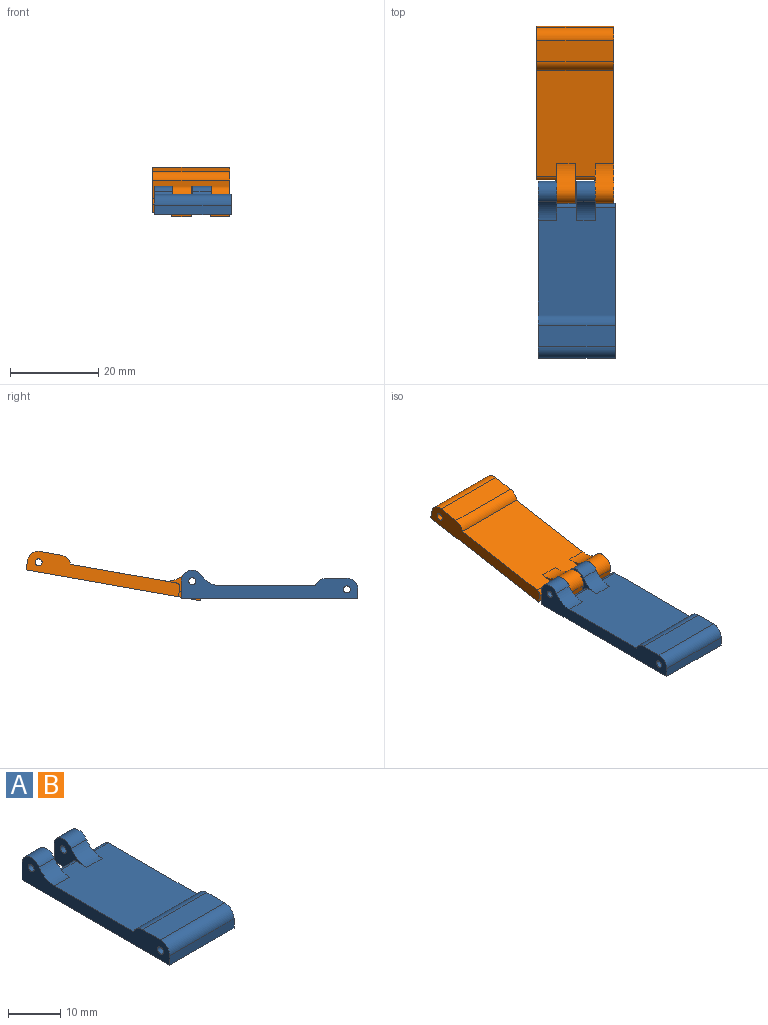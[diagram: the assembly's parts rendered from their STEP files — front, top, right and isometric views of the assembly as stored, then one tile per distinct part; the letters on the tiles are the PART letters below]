
ASSEMBLY  parts=2 mates=1
PART A: 28 faces, bbox 17.4x40x6.5 mm
  f0: plane 35x4.67mm, normal (1,0,0), area 116.5mm2, adj f2,f6,f8,f13,f14,f19,f21,f22
  f1: plane 4.35x4mm, normal (0,1,0), area 16.8mm2, adj f2,f4,f10,f11,f15,f26
  f2: plane 40x17.4mm, normal (0,0,-1), area 652.5mm2, adj f0,f1,f5,f6,f7,f11,f12,f13
  f3: plane 5x0.2mm, normal (0,0,1), area 1mm2, adj f5,f9,f12,f27
  f4: plane 5x0.2mm, normal (0,0,1), area 1mm2, adj f1,f10,f13,f26
  f5: plane 4.35x4mm, normal (0,1,0), area 16.8mm2, adj f2,f3,f7,f9,f16,f27
  f6: plane 17.4x2.17mm, normal (0,-1,0), area 37.7mm2, adj f0,f2,f7,f22
  f7: plane 40x6.5mm, normal (-1,0,0), area 146.7mm2, adj f2,f5,f6,f8,f14,f16,f18,f21
  f8: plane 24.3x17.4mm, normal (0,0,1), area 399.2mm2, adj f0,f7,f9,f10,f11,f17,f18,f19
  f9: plane 8.84x5.3mm, normal (1,0,0), area 24.2mm2, adj f3,f5,f8,f12,f16,f18,f20,f24
  f10: plane 8.84x5.3mm, normal (1,0,0), area 24.2mm2, adj f1,f4,f8,f13,f15,f17,f19,f23
  f11: plane 8.84x6.5mm, normal (-1,0,0), area 30.2mm2, adj f1,f2,f8,f12,f15,f17,f20,f23
  f12: plane 4.55x2mm, normal (0,1,0), area 8.9mm2, adj f2,f3,f9,f11,f20,f27
  f13: plane 4.55x2mm, normal (0,1,0), area 8.9mm2, adj f0,f2,f4,f10,f19,f26
  f14: plane 17.4x4.84mm, normal (0,0,1), area 84.3mm2, adj f0,f7,f21,f22
  f15: cylinder r=2.5mm len=4.61mm, axis (-1,0,0), area 26.8mm2, adj f1,f10,f11,f17
  f16: cylinder r=2.5mm len=4.61mm, axis (-1,0,0), area 26.8mm2, adj f5,f7,f9,f18
  f17: cylinder r=5mm len=4.23mm, axis (-1,0,0), area 20.9mm2, adj f8,f10,f11,f15
  f18: cylinder r=5mm len=4.23mm, axis (-1,0,0), area 20.9mm2, adj f7,f8,f9,f16
  f19: cylinder r=1mm len=4.55mm, axis (-1,0,0), area 7.1mm2, adj f0,f8,f10,f13
  f20: cylinder r=1mm len=4.55mm, axis (-1,0,0), area 7.1mm2, adj f8,f9,f11,f12
  f21: cylinder r=2.5mm len=17.4mm, axis (-1,0,0), area 53.5mm2, adj f0,f7,f8,f14
  f22: cylinder r=2.5mm len=17.4mm, axis (1,0,0), area 68.3mm2, adj f0,f6,f7,f14
  f23: cylinder r=0.8mm len=4.15mm, axis (-1,0,0), area 20.9mm2, adj f10,f11
  f24: cylinder r=0.8mm len=4.15mm, axis (-1,0,0), area 20.9mm2, adj f7,f9
  f25: cylinder r=0.8mm len=17.4mm, axis (-1,0,0), area 87.5mm2, adj f0,f7
  f26: plane 5x1.2mm, normal (1,0,0), area 6mm2, adj f1,f2,f4,f13
  f27: plane 5x1.2mm, normal (1,0,0), area 6mm2, adj f2,f3,f5,f12
PART B: same geometry as A
PLACE A t=(8.67,25.13,4.36)mm fixed
PLACE B rot(axis=(0,-0.09,1),180deg) t=(-92.73,11.02,3.13)mm
MATE revolute B.f15 <-> A.f15  axis (-1,0,0) through (-46.38,17.93,5.36)mm
